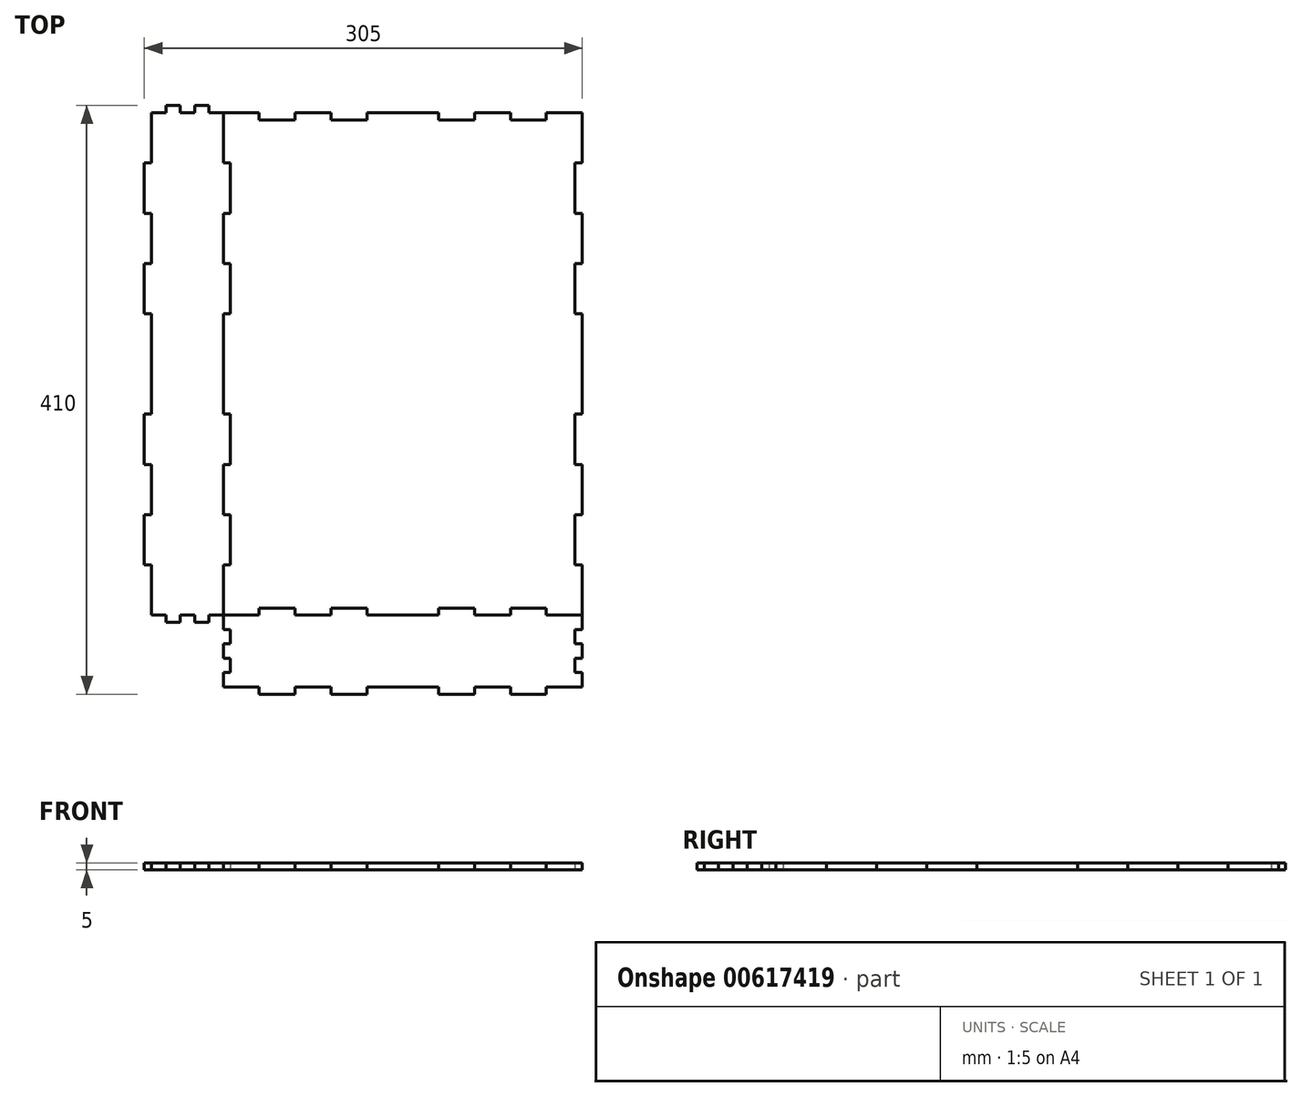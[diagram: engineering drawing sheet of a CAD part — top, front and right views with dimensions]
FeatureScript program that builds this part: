
annotation { "Feature Type Name" : "Feature", "Feature Type Description" : "" }
export const myFeature = defineFeature(function(context is Context, id is Id, definition is map)
    precondition{}
    {
        {
            assignVariable(context, id + "F0", {"name" : "thickness", "anyValue" : 5});
        }
        {
            var Q0;
            Q0=qCreatedBy(makeId("Top.planeOp"),FACE);
            var sketch = newSketch(context, id + "F1", { "sketchPlane" : qUnion([Q0])});
            skLineSegment(sketch, "E0.bottom", {"start": v(125, -175) * mm, "end": v(100, -175) * mm});
            skLineSegment(sketch, "E0.top", {"start": v(175, 175) * mm, "end": v(165, 175) * mm});
            skLineSegment(sketch, "E0.left", {"start": v(125, -175) * mm, "end": v(125, -140) * mm});
            skLineSegment(sketch, "E0.right", {"start": v(-125, -175) * mm, "end": v(-125, -140) * mm});
            skPoint(sketch, "E0.middle", {"position": v(0, 0) * mm});
            skLineSegment(sketch, "E1", {"start": v(0, 0) * mm, "end": v(0, 170) * mm, "construction": true});
            skLineSegment(sketch, "E2", {"start": v(-125, 0) * mm, "end": v(-125, 35) * mm});
            skLineSegment(sketch, "E3", {"start": v(0, 175) * mm, "end": v(-25, 175) * mm});
            skLineSegment(sketch, "E4", {"start": v(175, 175) * mm, "end": v(175, 140) * mm});
            skLineSegment(sketch, "E5", {"start": v(175, -175) * mm, "end": v(165, -175) * mm});
            skLineSegment(sketch, "E6", {"start": v(-175, 175) * mm, "end": v(-175, 140) * mm});
            skLineSegment(sketch, "E7", {"start": v(-175, -175) * mm, "end": v(-165, -175) * mm});
            skLineSegment(sketch, "E8", {"start": v(-125, 175) * mm, "end": v(-125, 185) * mm});
            skLineSegment(sketch, "E9", {"start": v(-125, 225) * mm, "end": v(-100, 225) * mm});
            skLineSegment(sketch, "E10", {"start": v(125, 225) * mm, "end": v(125, 215) * mm});
            skLineSegment(sketch, "E11", {"start": v(125, -175) * mm, "end": v(125, -185) * mm});
            skLineSegment(sketch, "E12", {"start": v(125, -225) * mm, "end": v(100, -225) * mm});
            skLineSegment(sketch, "E13", {"start": v(-125, -225) * mm, "end": v(-125, -215) * mm});
            skLineSegment(sketch, "E14", {"start": v(-100, 175) * mm, "end": v(-100, 170) * mm});
            skLineSegment(sketch, "E15", {"start": v(-100, 170) * mm, "end": v(-75, 170) * mm});
            skLineSegment(sketch, "E16", {"start": v(-75, 170) * mm, "end": v(-75, 175) * mm});
            skLineSegment(sketch, "E17", {"start": v(-125, 175) * mm, "end": v(-125, 175) * mm});
            skLineSegment(sketch, "E18", {"start": v(-100, 175) * mm, "end": v(-125, 175) * mm});
            skLineSegment(sketch, "E19.1.0.2", {"start": v(-75, 175) * mm, "end": v(-75, 170) * mm});
            skLineSegment(sketch, "E19.1.0.3", {"start": v(-50, 170) * mm, "end": v(-50, 175) * mm});
            skLineSegment(sketch, "E19.2.0.0", {"start": v(-50, 175) * mm, "end": v(-75, 175) * mm});
            skLineSegment(sketch, "E19.2.0.1", {"start": v(-50, 170) * mm, "end": v(-25, 170) * mm});
            skLineSegment(sketch, "E19.2.0.2", {"start": v(-50, 175) * mm, "end": v(-50, 170) * mm});
            skLineSegment(sketch, "E19.2.0.3", {"start": v(-25, 170) * mm, "end": v(-25, 175) * mm});
            skLineSegment(sketch, "E19.3.0.2", {"start": v(-25, 175) * mm, "end": v(-25, 170) * mm});
            skLineSegment(sketch, "E19.4.0.3", {"start": v(25, 170) * mm, "end": v(25, 175) * mm});
            skLineSegment(sketch, "E19.direction1", {"start": v(-125, 175) * mm, "end": v(-100, 175) * mm, "construction": true});
            skLineSegment(sketch, "E20.0.5.0", {"start": v(25, 175) * mm, "end": v(0, 175) * mm});
            skLineSegment(sketch, "E20.3.5.0", {"start": v(25, 170) * mm, "end": v(50, 170) * mm});
            skLineSegment(sketch, "E20.6.5.0", {"start": v(25, 175) * mm, "end": v(25, 170) * mm});
            skLineSegment(sketch, "E20.9.5.0", {"start": v(50, 170) * mm, "end": v(50, 175) * mm});
            skLineSegment(sketch, "E20.6.6.0", {"start": v(50, 175) * mm, "end": v(50, 170) * mm});
            skLineSegment(sketch, "E20.9.6.0", {"start": v(75, 170) * mm, "end": v(75, 175) * mm});
            skLineSegment(sketch, "E20.0.7.0", {"start": v(75, 175) * mm, "end": v(50, 175) * mm});
            skLineSegment(sketch, "E20.3.7.0", {"start": v(75, 170) * mm, "end": v(100, 170) * mm});
            skLineSegment(sketch, "E20.6.7.0", {"start": v(75, 175) * mm, "end": v(75, 170) * mm});
            skLineSegment(sketch, "E20.9.7.0", {"start": v(100, 170) * mm, "end": v(100, 175) * mm});
            skLineSegment(sketch, "E20.6.8.0", {"start": v(100, 175) * mm, "end": v(100, 170) * mm});
            skLineSegment(sketch, "E20.9.8.0", {"start": v(125, 170) * mm, "end": v(125, 175) * mm});
            skLineSegment(sketch, "E21", {"start": v(-125, 175) * mm, "end": v(-135, 175) * mm});
            skLineSegment(sketch, "E22", {"start": v(-75, 225) * mm, "end": v(-50, 225) * mm});
            skLineSegment(sketch, "E23", {"start": v(-125, 175) * mm, "end": v(-100, 175) * mm});
            skLineSegment(sketch, "E24", {"start": v(-100, 230) * mm, "end": v(-100, 225) * mm});
            skLineSegment(sketch, "E25", {"start": v(-100, 230) * mm, "end": v(-75, 230) * mm});
            skLineSegment(sketch, "E26", {"start": v(-75, 225) * mm, "end": v(-75, 230) * mm});
            skLineSegment(sketch, "E27.direction1", {"start": v(-125, 225) * mm, "end": v(-100, 225) * mm, "construction": true});
            skLineSegment(sketch, "E28", {"start": v(-100, -175) * mm, "end": v(-125, -175) * mm});
            skLineSegment(sketch, "E29", {"start": v(-100, -225) * mm, "end": v(-125, -225) * mm});
            skLineSegment(sketch, "E30", {"start": v(-100, -170) * mm, "end": v(-100, -175) * mm});
            skLineSegment(sketch, "E31", {"start": v(-100, -170) * mm, "end": v(-75, -170) * mm});
            skLineSegment(sketch, "E32", {"start": v(-75, -175) * mm, "end": v(-75, -170) * mm});
            skLineSegment(sketch, "E33", {"start": v(-75, -230) * mm, "end": v(-75, -225) * mm});
            skLineSegment(sketch, "E34", {"start": v(-75, -230) * mm, "end": v(-100, -230) * mm});
            skLineSegment(sketch, "E35", {"start": v(-100, -225) * mm, "end": v(-100, -230) * mm});
            skLineSegment(sketch, "E36.1.0.1", {"start": v(-75, -170) * mm, "end": v(-75, -175) * mm});
            skLineSegment(sketch, "E36.1.0.3", {"start": v(-50, -175) * mm, "end": v(-50, -170) * mm});
            skLineSegment(sketch, "E36.2.0.0", {"start": v(-50, -175) * mm, "end": v(-75, -175) * mm});
            skLineSegment(sketch, "E36.2.0.1", {"start": v(-50, -170) * mm, "end": v(-50, -175) * mm});
            skLineSegment(sketch, "E36.2.0.2", {"start": v(-50, -170) * mm, "end": v(-25, -170) * mm});
            skLineSegment(sketch, "E36.2.0.3", {"start": v(-25, -175) * mm, "end": v(-25, -170) * mm});
            skLineSegment(sketch, "E36.3.0.1", {"start": v(-25, -170) * mm, "end": v(-25, -175) * mm});
            skLineSegment(sketch, "E36.4.0.0", {"start": v(0, -175) * mm, "end": v(-25, -175) * mm});
            skLineSegment(sketch, "E36.4.0.3", {"start": v(25, -175) * mm, "end": v(25, -170) * mm});
            skLineSegment(sketch, "E36.5.0.0", {"start": v(25, -175) * mm, "end": v(0, -175) * mm});
            skLineSegment(sketch, "E36.5.0.1", {"start": v(25, -170) * mm, "end": v(25, -175) * mm});
            skLineSegment(sketch, "E36.5.0.2", {"start": v(25, -170) * mm, "end": v(50, -170) * mm});
            skLineSegment(sketch, "E36.5.0.3", {"start": v(50, -175) * mm, "end": v(50, -170) * mm});
            skLineSegment(sketch, "E36.6.0.1", {"start": v(50, -170) * mm, "end": v(50, -175) * mm});
            skLineSegment(sketch, "E36.6.0.3", {"start": v(75, -175) * mm, "end": v(75, -170) * mm});
            skLineSegment(sketch, "E36.7.0.0", {"start": v(75, -175) * mm, "end": v(50, -175) * mm});
            skLineSegment(sketch, "E36.7.0.1", {"start": v(75, -170) * mm, "end": v(75, -175) * mm});
            skLineSegment(sketch, "E36.7.0.2", {"start": v(75, -170) * mm, "end": v(100, -170) * mm});
            skLineSegment(sketch, "E36.7.0.3", {"start": v(100, -175) * mm, "end": v(100, -170) * mm});
            skLineSegment(sketch, "E36.8.0.1", {"start": v(100, -170) * mm, "end": v(100, -175) * mm});
            skLineSegment(sketch, "E36.8.0.3", {"start": v(125, -175) * mm, "end": v(125, -170) * mm});
            skLineSegment(sketch, "E36.direction1", {"start": v(-125, -175) * mm, "end": v(-100, -175) * mm, "construction": true});
            skLineSegment(sketch, "E37.1.0.1", {"start": v(-75, -225) * mm, "end": v(-75, -230) * mm});
            skLineSegment(sketch, "E37.1.0.3", {"start": v(-50, -230) * mm, "end": v(-50, -225) * mm});
            skLineSegment(sketch, "E37.2.0.0", {"start": v(-50, -225) * mm, "end": v(-75, -225) * mm});
            skLineSegment(sketch, "E37.2.0.1", {"start": v(-50, -225) * mm, "end": v(-50, -230) * mm});
            skLineSegment(sketch, "E37.2.0.2", {"start": v(-25, -230) * mm, "end": v(-50, -230) * mm});
            skLineSegment(sketch, "E37.2.0.3", {"start": v(-25, -230) * mm, "end": v(-25, -225) * mm});
            skLineSegment(sketch, "E37.3.0.1", {"start": v(-25, -225) * mm, "end": v(-25, -230) * mm});
            skLineSegment(sketch, "E37.4.0.0", {"start": v(0, -225) * mm, "end": v(-25, -225) * mm});
            skLineSegment(sketch, "E37.4.0.3", {"start": v(25, -230) * mm, "end": v(25, -225) * mm});
            skLineSegment(sketch, "E37.5.0.0", {"start": v(25, -225) * mm, "end": v(0, -225) * mm});
            skLineSegment(sketch, "E37.5.0.1", {"start": v(25, -225) * mm, "end": v(25, -230) * mm});
            skLineSegment(sketch, "E37.5.0.2", {"start": v(50, -230) * mm, "end": v(25, -230) * mm});
            skLineSegment(sketch, "E37.5.0.3", {"start": v(50, -230) * mm, "end": v(50, -225) * mm});
            skLineSegment(sketch, "E37.6.0.1", {"start": v(50, -225) * mm, "end": v(50, -230) * mm});
            skLineSegment(sketch, "E37.6.0.3", {"start": v(75, -230) * mm, "end": v(75, -225) * mm});
            skLineSegment(sketch, "E37.7.0.0", {"start": v(75, -225) * mm, "end": v(50, -225) * mm});
            skLineSegment(sketch, "E37.7.0.1", {"start": v(75, -225) * mm, "end": v(75, -230) * mm});
            skLineSegment(sketch, "E37.7.0.2", {"start": v(100, -230) * mm, "end": v(75, -230) * mm});
            skLineSegment(sketch, "E37.7.0.3", {"start": v(100, -230) * mm, "end": v(100, -225) * mm});
            skLineSegment(sketch, "E37.8.0.1", {"start": v(100, -225) * mm, "end": v(100, -230) * mm});
            skLineSegment(sketch, "E37.direction1", {"start": v(-125, -225) * mm, "end": v(-100, -225) * mm, "construction": true});
            skLineSegment(sketch, "E38", {"start": v(125, 140) * mm, "end": v(125, 175) * mm});
            skLineSegment(sketch, "E39", {"start": v(175, 105) * mm, "end": v(175, 70) * mm});
            skLineSegment(sketch, "E40", {"start": v(125, 140) * mm, "end": v(120, 140) * mm});
            skLineSegment(sketch, "E41", {"start": v(120, 140) * mm, "end": v(120, 105) * mm});
            skLineSegment(sketch, "E42", {"start": v(120, 105) * mm, "end": v(125, 105) * mm});
            skLineSegment(sketch, "E43", {"start": v(175, 140) * mm, "end": v(180, 140) * mm});
            skLineSegment(sketch, "E44", {"start": v(180, 140) * mm, "end": v(180, 105) * mm});
            skLineSegment(sketch, "E45", {"start": v(180, 105) * mm, "end": v(175, 105) * mm});
            skLineSegment(sketch, "E46.0.1.0", {"start": v(125, 105) * mm, "end": v(120, 105) * mm});
            skLineSegment(sketch, "E46.0.1.2", {"start": v(120, 70) * mm, "end": v(125, 70) * mm});
            skLineSegment(sketch, "E46.0.2.0", {"start": v(125, 70) * mm, "end": v(120, 70) * mm});
            skLineSegment(sketch, "E46.0.2.1", {"start": v(120, 70) * mm, "end": v(120, 35) * mm});
            skLineSegment(sketch, "E46.0.2.2", {"start": v(120, 35) * mm, "end": v(125, 35) * mm});
            skLineSegment(sketch, "E46.0.3.0", {"start": v(125, 35) * mm, "end": v(120, 35) * mm});
            skLineSegment(sketch, "E46.0.4.2", {"start": v(120, -35) * mm, "end": v(125, -35) * mm});
            skLineSegment(sketch, "E46.0.5.0", {"start": v(125, -35) * mm, "end": v(120, -35) * mm});
            skLineSegment(sketch, "E46.0.5.1", {"start": v(120, -35) * mm, "end": v(120, -70) * mm});
            skLineSegment(sketch, "E46.0.5.2", {"start": v(120, -70) * mm, "end": v(125, -70) * mm});
            skLineSegment(sketch, "E46.0.6.0", {"start": v(125, -70) * mm, "end": v(120, -70) * mm});
            skLineSegment(sketch, "E46.0.6.2", {"start": v(120, -105) * mm, "end": v(125, -105) * mm});
            skLineSegment(sketch, "E46.0.7.0", {"start": v(125, -105) * mm, "end": v(120, -105) * mm});
            skLineSegment(sketch, "E46.0.7.1", {"start": v(120, -105) * mm, "end": v(120, -140) * mm});
            skLineSegment(sketch, "E46.0.7.2", {"start": v(120, -140) * mm, "end": v(125, -140) * mm});
            skLineSegment(sketch, "E46.0.8.0", {"start": v(125, -140) * mm, "end": v(120, -140) * mm});
            skLineSegment(sketch, "E46.0.8.2", {"start": v(120, -175) * mm, "end": v(125, -175) * mm});
            skLineSegment(sketch, "E46.direction1", {"start": v(120, 105) * mm, "end": v(145, 105) * mm, "construction": true});
            skLineSegment(sketch, "E47.0.1.0", {"start": v(175, 105) * mm, "end": v(180, 105) * mm});
            skLineSegment(sketch, "E47.0.1.2", {"start": v(180, 70) * mm, "end": v(175, 70) * mm});
            skLineSegment(sketch, "E47.0.2.0", {"start": v(175, 70) * mm, "end": v(180, 70) * mm});
            skLineSegment(sketch, "E47.0.2.1", {"start": v(180, 70) * mm, "end": v(180, 35) * mm});
            skLineSegment(sketch, "E47.0.2.2", {"start": v(180, 35) * mm, "end": v(175, 35) * mm});
            skLineSegment(sketch, "E47.0.3.0", {"start": v(175, 35) * mm, "end": v(180, 35) * mm});
            skLineSegment(sketch, "E47.0.4.2", {"start": v(180, -35) * mm, "end": v(175, -35) * mm});
            skLineSegment(sketch, "E47.0.5.0", {"start": v(175, -35) * mm, "end": v(180, -35) * mm});
            skLineSegment(sketch, "E47.0.5.1", {"start": v(180, -35) * mm, "end": v(180, -70) * mm});
            skLineSegment(sketch, "E47.0.5.2", {"start": v(180, -70) * mm, "end": v(175, -70) * mm});
            skLineSegment(sketch, "E47.0.6.0", {"start": v(175, -70) * mm, "end": v(180, -70) * mm});
            skLineSegment(sketch, "E47.0.6.2", {"start": v(180, -105) * mm, "end": v(175, -105) * mm});
            skLineSegment(sketch, "E47.0.7.0", {"start": v(175, -105) * mm, "end": v(180, -105) * mm});
            skLineSegment(sketch, "E47.0.7.1", {"start": v(180, -105) * mm, "end": v(180, -140) * mm});
            skLineSegment(sketch, "E47.0.7.2", {"start": v(180, -140) * mm, "end": v(175, -140) * mm});
            skLineSegment(sketch, "E47.0.8.0", {"start": v(175, -140) * mm, "end": v(180, -140) * mm});
            skLineSegment(sketch, "E47.direction1", {"start": v(175, 105) * mm, "end": v(200, 105) * mm, "construction": true});
            skLineSegment(sketch, "E47.direction2", {"start": v(175, 105) * mm, "end": v(175, 70) * mm, "construction": true});
            skLineSegment(sketch, "E48", {"start": v(-125, 140) * mm, "end": v(-125, 175) * mm});
            skLineSegment(sketch, "E49", {"start": v(-175, 105) * mm, "end": v(-175, 70) * mm});
            skLineSegment(sketch, "E50", {"start": v(-125, 140) * mm, "end": v(-120, 140) * mm});
            skLineSegment(sketch, "E51", {"start": v(-120, 140) * mm, "end": v(-120, 105) * mm});
            skLineSegment(sketch, "E52", {"start": v(-120, 105) * mm, "end": v(-125, 105) * mm});
            skLineSegment(sketch, "E53", {"start": v(-175, 140) * mm, "end": v(-180, 140) * mm});
            skLineSegment(sketch, "E54", {"start": v(-180, 140) * mm, "end": v(-180, 105) * mm});
            skLineSegment(sketch, "E55", {"start": v(-180, 105) * mm, "end": v(-175, 105) * mm});
            skLineSegment(sketch, "E56.0.1.0", {"start": v(-175, 105) * mm, "end": v(-180, 105) * mm});
            skLineSegment(sketch, "E56.0.1.2", {"start": v(-180, 70) * mm, "end": v(-175, 70) * mm});
            skLineSegment(sketch, "E56.0.2.0", {"start": v(-175, 70) * mm, "end": v(-180, 70) * mm});
            skLineSegment(sketch, "E56.0.2.1", {"start": v(-180, 70) * mm, "end": v(-180, 35) * mm});
            skLineSegment(sketch, "E56.0.2.2", {"start": v(-180, 35) * mm, "end": v(-175, 35) * mm});
            skLineSegment(sketch, "E56.0.3.0", {"start": v(-175, 35) * mm, "end": v(-180, 35) * mm});
            skLineSegment(sketch, "E56.0.4.2", {"start": v(-180, -35) * mm, "end": v(-175, -35) * mm});
            skLineSegment(sketch, "E56.0.5.0", {"start": v(-175, -35) * mm, "end": v(-180, -35) * mm});
            skLineSegment(sketch, "E56.0.5.1", {"start": v(-180, -35) * mm, "end": v(-180, -70) * mm});
            skLineSegment(sketch, "E56.0.5.2", {"start": v(-180, -70) * mm, "end": v(-175, -70) * mm});
            skLineSegment(sketch, "E56.0.6.0", {"start": v(-175, -70) * mm, "end": v(-180, -70) * mm});
            skLineSegment(sketch, "E56.0.6.2", {"start": v(-180, -105) * mm, "end": v(-175, -105) * mm});
            skLineSegment(sketch, "E56.0.7.0", {"start": v(-175, -105) * mm, "end": v(-180, -105) * mm});
            skLineSegment(sketch, "E56.0.7.1", {"start": v(-180, -105) * mm, "end": v(-180, -140) * mm});
            skLineSegment(sketch, "E56.0.7.2", {"start": v(-180, -140) * mm, "end": v(-175, -140) * mm});
            skLineSegment(sketch, "E56.0.8.0", {"start": v(-175, -140) * mm, "end": v(-180, -140) * mm});
            skLineSegment(sketch, "E56.direction1", {"start": v(-180, 105) * mm, "end": v(-155, 105) * mm, "construction": true});
            skLineSegment(sketch, "E57.0.1.0", {"start": v(-125, 105) * mm, "end": v(-120, 105) * mm});
            skLineSegment(sketch, "E57.0.1.2", {"start": v(-120, 70) * mm, "end": v(-125, 70) * mm});
            skLineSegment(sketch, "E57.0.2.0", {"start": v(-125, 70) * mm, "end": v(-120, 70) * mm});
            skLineSegment(sketch, "E57.0.2.1", {"start": v(-120, 70) * mm, "end": v(-120, 35) * mm});
            skLineSegment(sketch, "E57.0.2.2", {"start": v(-120, 35) * mm, "end": v(-125, 35) * mm});
            skLineSegment(sketch, "E57.0.3.0", {"start": v(-125, 35) * mm, "end": v(-120, 35) * mm});
            skLineSegment(sketch, "E57.0.4.2", {"start": v(-120, -35) * mm, "end": v(-125, -35) * mm});
            skLineSegment(sketch, "E57.0.5.0", {"start": v(-125, -35) * mm, "end": v(-120, -35) * mm});
            skLineSegment(sketch, "E57.0.5.1", {"start": v(-120, -35) * mm, "end": v(-120, -70) * mm});
            skLineSegment(sketch, "E57.0.5.2", {"start": v(-120, -70) * mm, "end": v(-125, -70) * mm});
            skLineSegment(sketch, "E57.0.6.0", {"start": v(-125, -70) * mm, "end": v(-120, -70) * mm});
            skLineSegment(sketch, "E57.0.6.2", {"start": v(-120, -105) * mm, "end": v(-125, -105) * mm});
            skLineSegment(sketch, "E57.0.7.0", {"start": v(-125, -105) * mm, "end": v(-120, -105) * mm});
            skLineSegment(sketch, "E57.0.7.1", {"start": v(-120, -105) * mm, "end": v(-120, -140) * mm});
            skLineSegment(sketch, "E57.0.7.2", {"start": v(-120, -140) * mm, "end": v(-125, -140) * mm});
            skLineSegment(sketch, "E57.0.8.0", {"start": v(-125, -140) * mm, "end": v(-120, -140) * mm});
            skLineSegment(sketch, "E57.0.8.2", {"start": v(-120, -175) * mm, "end": v(-125, -175) * mm});
            skLineSegment(sketch, "E57.direction1", {"start": v(-125, 105) * mm, "end": v(-100, 105) * mm, "construction": true});
            skLineSegment(sketch, "E57.direction2", {"start": v(-125, 105) * mm, "end": v(-125, 70) * mm, "construction": true});
            skLineSegment(sketch, "E58", {"start": v(135, -175) * mm, "end": v(125, -175) * mm});
            skLineSegment(sketch, "E59", {"start": v(135, -175) * mm, "end": v(135, -180) * mm});
            skLineSegment(sketch, "E60", {"start": v(135, -180) * mm, "end": v(145, -180) * mm});
            skLineSegment(sketch, "E61", {"start": v(145, -180) * mm, "end": v(145, -175) * mm});
            skLineSegment(sketch, "E62", {"start": v(125, -195) * mm, "end": v(125, -205) * mm});
            skLineSegment(sketch, "E63", {"start": v(125, 105) * mm, "end": v(125, 70) * mm});
            skLineSegment(sketch, "E64", {"start": v(125, 35) * mm, "end": v(125, -35) * mm});
            skLineSegment(sketch, "E65", {"start": v(125, -70) * mm, "end": v(125, -105) * mm});
            skLineSegment(sketch, "E66.trimOffspring", {"start": v(175, 35) * mm, "end": v(175, -35) * mm});
            skLineSegment(sketch, "E67.trimOffspring", {"start": v(175, -70) * mm, "end": v(175, -105) * mm});
            skLineSegment(sketch, "E68.trimOffspring", {"start": v(175, -140) * mm, "end": v(175, -175) * mm});
            skLineSegment(sketch, "E69.trimOffspring", {"start": v(-125, -35) * mm, "end": v(-125, 0) * mm});
            skLineSegment(sketch, "E70.trimOffspring", {"start": v(-125, -105) * mm, "end": v(-125, -70) * mm});
            skLineSegment(sketch, "E71.trimOffspring", {"start": v(-175, -70) * mm, "end": v(-175, -105) * mm});
            skLineSegment(sketch, "E72.trimOffspring", {"start": v(-175, -140) * mm, "end": v(-175, -175) * mm});
            skLineSegment(sketch, "E73.trimOffspring", {"start": v(-125, 70) * mm, "end": v(-125, 105) * mm});
            skLineSegment(sketch, "E74.trimOffspring", {"start": v(-175, 35) * mm, "end": v(-175, -35) * mm});
            skLineSegment(sketch, "E75.trimOffspring", {"start": v(0, 175) * mm, "end": v(0, 225) * mm, "construction": true});
            skLineSegment(sketch, "E76.3.1.0", {"start": v(-75, 230) * mm, "end": v(-75, 225) * mm});
            skLineSegment(sketch, "E76.9.1.0", {"start": v(-50, 225) * mm, "end": v(-50, 230) * mm});
            skLineSegment(sketch, "E76.3.2.0", {"start": v(-50, 230) * mm, "end": v(-50, 225) * mm});
            skLineSegment(sketch, "E76.6.2.0", {"start": v(-50, 230) * mm, "end": v(-25, 230) * mm});
            skLineSegment(sketch, "E76.9.2.0", {"start": v(-25, 225) * mm, "end": v(-25, 230) * mm});
            skLineSegment(sketch, "E76.3.3.0", {"start": v(-25, 230) * mm, "end": v(-25, 225) * mm});
            skLineSegment(sketch, "E76.0.4.0", {"start": v(-25, 225) * mm, "end": v(0, 225) * mm});
            skLineSegment(sketch, "E76.9.4.0", {"start": v(25, 225) * mm, "end": v(25, 230) * mm});
            skLineSegment(sketch, "E76.0.5.0", {"start": v(0, 225) * mm, "end": v(25, 225) * mm});
            skLineSegment(sketch, "E76.3.5.0", {"start": v(25, 230) * mm, "end": v(25, 225) * mm});
            skLineSegment(sketch, "E76.6.5.0", {"start": v(25, 230) * mm, "end": v(50, 230) * mm});
            skLineSegment(sketch, "E76.9.5.0", {"start": v(50, 225) * mm, "end": v(50, 230) * mm});
            skLineSegment(sketch, "E76.3.6.0", {"start": v(50, 230) * mm, "end": v(50, 225) * mm});
            skLineSegment(sketch, "E76.9.6.0", {"start": v(75, 225) * mm, "end": v(75, 230) * mm});
            skLineSegment(sketch, "E76.0.7.0", {"start": v(50, 225) * mm, "end": v(75, 225) * mm});
            skLineSegment(sketch, "E76.3.7.0", {"start": v(75, 230) * mm, "end": v(75, 225) * mm});
            skLineSegment(sketch, "E76.6.7.0", {"start": v(75, 230) * mm, "end": v(100, 230) * mm});
            skLineSegment(sketch, "E76.9.7.0", {"start": v(100, 225) * mm, "end": v(100, 230) * mm});
            skLineSegment(sketch, "E77.trimOffspring", {"start": v(-25, 225) * mm, "end": v(25, 225) * mm});
            skLineSegment(sketch, "E78.trimOffspring", {"start": v(100, 225) * mm, "end": v(125, 225) * mm});
            skLineSegment(sketch, "E79.trimOffspring", {"start": v(25, -225) * mm, "end": v(-25, -225) * mm});
            skLineSegment(sketch, "E80.1.0.0", {"start": v(165, -180) * mm, "end": v(165, -175) * mm});
            skLineSegment(sketch, "E80.1.0.1", {"start": v(155, -180) * mm, "end": v(165, -180) * mm});
            skLineSegment(sketch, "E80.1.0.2", {"start": v(155, -175) * mm, "end": v(155, -180) * mm});
            skLineSegment(sketch, "E80.direction1", {"start": v(135, -180) * mm, "end": v(155, -180) * mm, "construction": true});
            skLineSegment(sketch, "E81", {"start": v(125, -185) * mm, "end": v(120, -185) * mm});
            skLineSegment(sketch, "E82", {"start": v(120, -185) * mm, "end": v(120, -195) * mm});
            skLineSegment(sketch, "E83", {"start": v(120, -195) * mm, "end": v(125, -195) * mm});
            skLineSegment(sketch, "E84.0.1.0", {"start": v(125, -205) * mm, "end": v(120, -205) * mm});
            skLineSegment(sketch, "E84.0.1.1", {"start": v(120, -205) * mm, "end": v(120, -215) * mm});
            skLineSegment(sketch, "E84.0.1.2", {"start": v(120, -215) * mm, "end": v(125, -215) * mm});
            skLineSegment(sketch, "E84.direction1", {"start": v(120, -195) * mm, "end": v(145, -195) * mm, "construction": true});
            skLineSegment(sketch, "E84.direction2", {"start": v(120, -195) * mm, "end": v(120, -215) * mm, "construction": true});
            skLineSegment(sketch, "E85.trimOffspring", {"start": v(125, -215) * mm, "end": v(125, -225) * mm});
            skLineSegment(sketch, "E86", {"start": v(-125, -185) * mm, "end": v(-125, -175) * mm});
            skLineSegment(sketch, "E87", {"start": v(-120, -185) * mm, "end": v(-125, -185) * mm});
            skLineSegment(sketch, "E88", {"start": v(-120, -185) * mm, "end": v(-120, -195) * mm});
            skLineSegment(sketch, "E89", {"start": v(-125, -195) * mm, "end": v(-120, -195) * mm});
            skLineSegment(sketch, "E90.0.1.0", {"start": v(-120, -205) * mm, "end": v(-125, -205) * mm});
            skLineSegment(sketch, "E90.0.1.1", {"start": v(-120, -205) * mm, "end": v(-120, -215) * mm});
            skLineSegment(sketch, "E90.0.1.2", {"start": v(-125, -215) * mm, "end": v(-120, -215) * mm});
            skLineSegment(sketch, "E90.direction1", {"start": v(-125, -195) * mm, "end": v(-100, -195) * mm, "construction": true});
            skLineSegment(sketch, "E90.direction2", {"start": v(-125, -195) * mm, "end": v(-125, -205) * mm, "construction": true});
            skLineSegment(sketch, "E91.trimOffspring", {"start": v(-125, -205) * mm, "end": v(-125, -195) * mm});
            skLineSegment(sketch, "E92.trimOffspring", {"start": v(155, -175) * mm, "end": v(145, -175) * mm});
            skLineSegment(sketch, "E93", {"start": v(135, 175) * mm, "end": v(125, 175) * mm});
            skLineSegment(sketch, "E94", {"start": v(155, 175) * mm, "end": v(145, 175) * mm});
            skLineSegment(sketch, "E95", {"start": v(135, 175) * mm, "end": v(135, 180) * mm});
            skLineSegment(sketch, "E96", {"start": v(135, 180) * mm, "end": v(145, 180) * mm});
            skLineSegment(sketch, "E97", {"start": v(145, 180) * mm, "end": v(145, 175) * mm});
            skLineSegment(sketch, "E98", {"start": v(155, 175) * mm, "end": v(155, 180) * mm});
            skLineSegment(sketch, "E99", {"start": v(155, 180) * mm, "end": v(165, 180) * mm});
            skLineSegment(sketch, "E100", {"start": v(165, 180) * mm, "end": v(165, 175) * mm});
            skLineSegment(sketch, "E101", {"start": v(125, 185) * mm, "end": v(125, 175) * mm});
            skLineSegment(sketch, "E102", {"start": v(125, 175) * mm, "end": v(100, 175) * mm});
            skLineSegment(sketch, "E103", {"start": v(125, 205) * mm, "end": v(125, 195) * mm});
            skLineSegment(sketch, "E104", {"start": v(125, 215) * mm, "end": v(120, 215) * mm});
            skLineSegment(sketch, "E105", {"start": v(120, 215) * mm, "end": v(120, 205) * mm});
            skLineSegment(sketch, "E106", {"start": v(120, 205) * mm, "end": v(125, 205) * mm});
            skLineSegment(sketch, "E107", {"start": v(125, 195) * mm, "end": v(120, 195) * mm});
            skLineSegment(sketch, "E108", {"start": v(120, 195) * mm, "end": v(120, 185) * mm});
            skLineSegment(sketch, "E109", {"start": v(120, 185) * mm, "end": v(125, 185) * mm});
            skLineSegment(sketch, "E110", {"start": v(-155, -175) * mm, "end": v(-145, -175) * mm});
            skLineSegment(sketch, "E111", {"start": v(-135, -175) * mm, "end": v(-125, -175) * mm});
            skLineSegment(sketch, "E112", {"start": v(-135, -175) * mm, "end": v(-135, -180) * mm});
            skLineSegment(sketch, "E113", {"start": v(-135, -180) * mm, "end": v(-145, -180) * mm});
            skLineSegment(sketch, "E114", {"start": v(-145, -180) * mm, "end": v(-135, -179.9) * mm});
            skLineSegment(sketch, "E115", {"start": v(-145, -180) * mm, "end": v(-145, -175) * mm});
            skLineSegment(sketch, "E116", {"start": v(-155, -175) * mm, "end": v(-155, -180) * mm});
            skLineSegment(sketch, "E117", {"start": v(-155, -180) * mm, "end": v(-165, -180) * mm});
            skLineSegment(sketch, "E118", {"start": v(-165, -180) * mm, "end": v(-165, -175) * mm});
            skLineSegment(sketch, "E119", {"start": v(-165, 175) * mm, "end": v(-175, 175) * mm});
            skLineSegment(sketch, "E120", {"start": v(-145, 175) * mm, "end": v(-155, 175) * mm});
            skLineSegment(sketch, "E121", {"start": v(-125, 195) * mm, "end": v(-125, 205) * mm});
            skLineSegment(sketch, "E122", {"start": v(-125, 215) * mm, "end": v(-125, 225) * mm});
            skLineSegment(sketch, "E123", {"start": v(-165, 175) * mm, "end": v(-165, 180) * mm});
            skLineSegment(sketch, "E124", {"start": v(-165, 180) * mm, "end": v(-155, 180) * mm});
            skLineSegment(sketch, "E125", {"start": v(-155, 180) * mm, "end": v(-155, 175) * mm});
            skLineSegment(sketch, "E126", {"start": v(-145, 175) * mm, "end": v(-145, 180) * mm});
            skLineSegment(sketch, "E127", {"start": v(-145, 180) * mm, "end": v(-135, 180) * mm});
            skLineSegment(sketch, "E128", {"start": v(-135, 180) * mm, "end": v(-135, 175) * mm});
            skLineSegment(sketch, "E129", {"start": v(-125, 185) * mm, "end": v(-120, 185) * mm});
            skLineSegment(sketch, "E130", {"start": v(-120, 185) * mm, "end": v(-120, 195) * mm});
            skLineSegment(sketch, "E131", {"start": v(-120, 195) * mm, "end": v(-125, 195) * mm});
            skLineSegment(sketch, "E132", {"start": v(-125, 205) * mm, "end": v(-120, 205) * mm});
            skLineSegment(sketch, "E133", {"start": v(-120, 205) * mm, "end": v(-120, 215) * mm});
            skLineSegment(sketch, "E134", {"start": v(-120, 215) * mm, "end": v(-125, 215) * mm});
            skSolve(sketch);
        }
        {
            var Q0;
            Q0=makeQuery(id+"F1.imprint","IMPRINT",FACE,{"disambiguationData":[TD([[makeQuery(id+"F1.imprint","IMPRINT",EDGE,{"derivedFrom":sQuery(id+"F1.wireOp",EDGE,"E0.bottom")}),-1.0]])]});
            extrude(context, id + "F2", {"entities" : qUnion([Q0]), "depth" : (getVariable(context, 'thickness')) * mm, "offsetDistance" : 25 * mm});
        }
        {
            var Q0;
            Q0=makeQuery(id+"F1.imprint","IMPRINT",FACE,{"disambiguationData":[TD([[makeQuery(id+"F1.imprint","IMPRINT",EDGE,{"derivedFrom":sQuery(id+"F1.wireOp",EDGE,"E0.right")}),1.0]])]});
            extrude(context, id + "F3", {"entities" : qUnion([Q0]), "depth" : (getVariable(context, 'thickness')) * mm, "offsetDistance" : 25 * mm});
        }
        {
            var Q0;
            Q0=makeQuery(id+"F1.imprint","IMPRINT",FACE,{"disambiguationData":[TD([[makeQuery(id+"F1.imprint","IMPRINT",EDGE,{"derivedFrom":sQuery(id+"F1.wireOp",EDGE,"E0.bottom")}),1.0]])]});
            extrude(context, id + "F4", {"entities" : qUnion([Q0]), "depth" : (getVariable(context, 'thickness')) * mm, "offsetDistance" : 25 * mm});
        }
    });
